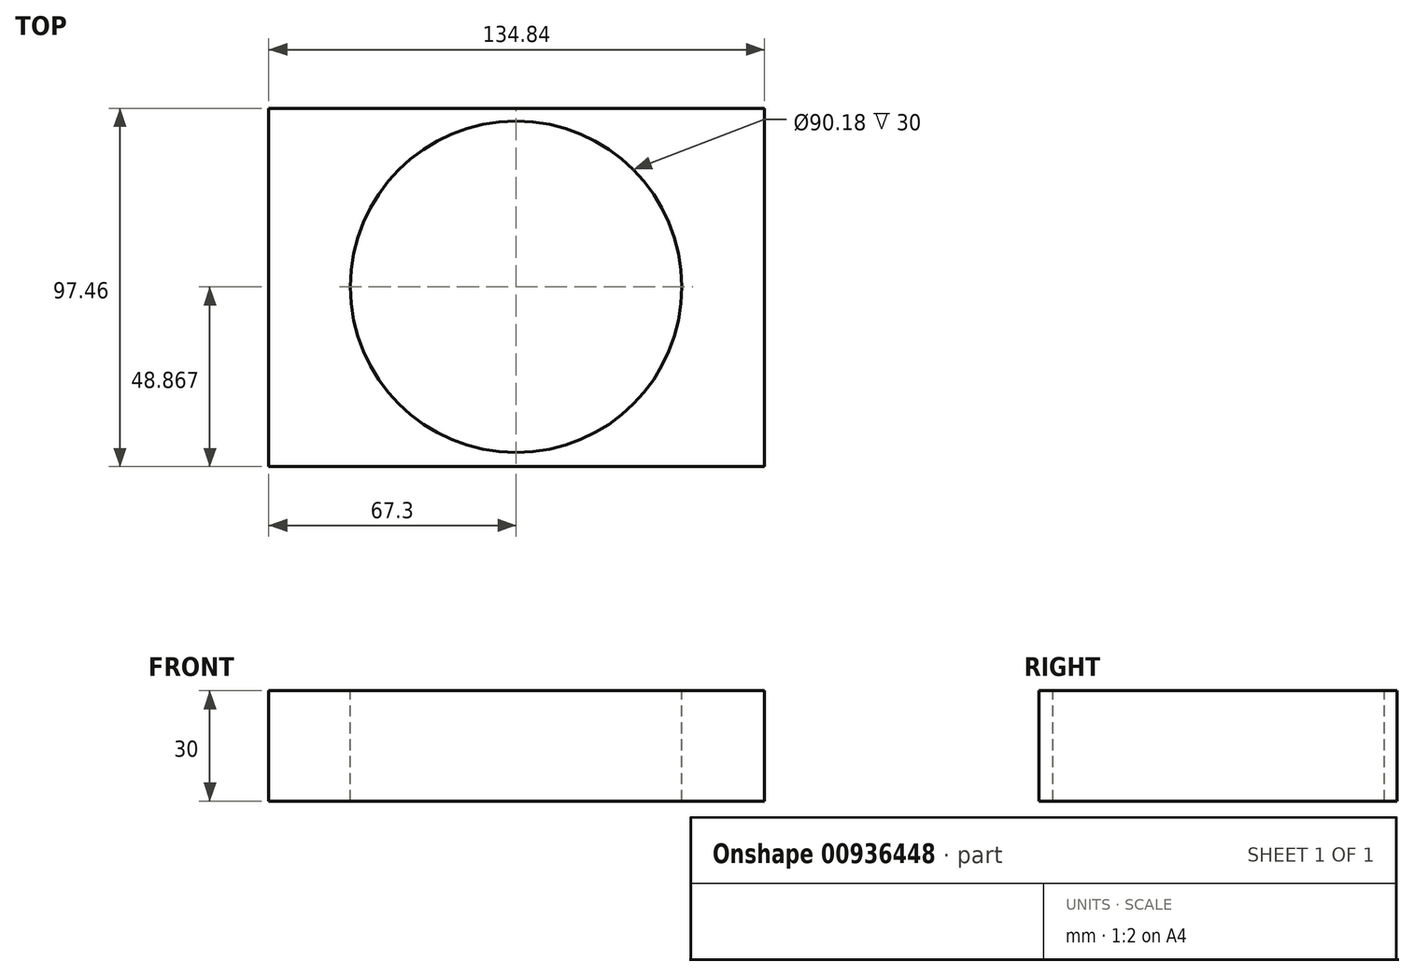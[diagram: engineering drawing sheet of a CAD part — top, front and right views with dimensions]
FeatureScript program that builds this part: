
annotation { "Feature Type Name" : "Feature", "Feature Type Description" : "" }
export const myFeature = defineFeature(function(context is Context, id is Id, definition is map)
    precondition{}
    {
        {
            var Q0;
            Q0=qCreatedBy(makeId("Top.planeOp"),FACE);
            var sketch = newSketch(context, id + "F0", { "sketchPlane" : qUnion([Q0])});
            skLineSegment(sketch, "E0.bottom", {"start": v(-67.42, 48.73) * mm, "end": v(67.42, 48.73) * mm});
            skLineSegment(sketch, "E0.top", {"start": v(-67.42, -48.73) * mm, "end": v(67.42, -48.73) * mm});
            skLineSegment(sketch, "E0.left", {"start": v(-67.42, 48.73) * mm, "end": v(-67.42, -48.73) * mm});
            skLineSegment(sketch, "E0.right", {"start": v(67.42, 48.73) * mm, "end": v(67.42, -48.73) * mm});
            skPoint(sketch, "E0.middle", {"position": v(0, 0) * mm});
            skSolve(sketch);
        }
        {
            var Q0;
            Q0=makeQuery(id+"F0.imprint","IMPRINT",FACE,{"disambiguationData":[TD([[makeQuery(id+"F0.imprint","IMPRINT",EDGE,{"derivedFrom":sQuery(id+"F0.wireOp",EDGE,"E0.bottom")}),-1.0]])]});
            extrude(context, id + "F1", {"entities" : qUnion([Q0]), "depth" : 30 * mm, "offsetDistance" : 25 * mm});
        }
        {
            var Q0;
            Q0=makeQuery(id+"F1.opExtrude","CAP_FACE",FACE,{"disambiguationData":[OSD([sQuery(id+"F0.wireOp",EDGE,"E0.bottom"),sQuery(id+"F0.wireOp",EDGE,"E0.top"),sQuery(id+"F0.wireOp",EDGE,"E0.left"),sQuery(id+"F0.wireOp",EDGE,"E0.right")])],"isStart":false});
            var sketch = newSketch(context, id + "F2", { "sketchPlane" : qUnion([Q0])});
            skCircle(sketch, "E1", {"center": v(-0.12, 0.14) * mm, "radius": 45.09 * mm});
            skSolve(sketch);
        }
        {
            var Q0;
            Q0=makeQuery(id+"F2.imprint","IMPRINT",FACE,{"disambiguationData":[TD([[makeQuery(id+"F2.imprint","IMPRINT",EDGE,{"derivedFrom":sQuery(id+"F2.wireOp",EDGE,"E1")}),1.0]])]});
            var Q1;
            Q1=sQuery(id+"F2.wireOp",EDGE,"E1");
            extrude(context, id + "F3", {"entities" : qUnion([Q0]), "operationType" : NewBodyOperationType.REMOVE, "surfaceEntities" : qUnion([Q1]), "oppositeDirection" : true, "depth" : 30 * mm, "offsetDistance" : 25 * mm});
        }
    });
